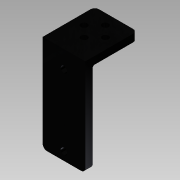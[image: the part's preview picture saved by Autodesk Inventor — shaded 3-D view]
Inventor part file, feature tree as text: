
AUTODESK INVENTOR PART (.ipt)
format: ipt  version: 2015 SP1 (Build 190203100, 203)  size: 181,760 bytes
history: native  units: mm
features: sketch x8, extrude x6, projected_geometry x3, sweep x1, fillet x1
ambient origin geometry x8: Origin, YZ Plane, XZ Plane, XY Plane, X Axis, Y Axis, Z Axis, Center Point
bodies: Solid1 (feature_tree)
feature tree (19):
  extrude  "Extrusion1"  Depth=20.0mm
  sweep  "Sweep1"
  extrude  "Extrusion2"  TaperAngle=0.0deg  [1 undecoded]
  fillet  "Fillet1"  Radius=20.0mm
  extrude  "Extrusion3"  Depth=1.0mm
  extrude  "Extrusion4"  Depth=3.0mm
  extrude  "Extrusion5"  Depth=2.0mm TaperAngle=0.0deg
  extrude  "Extrusion6"  Depth=2.0mm
  sketch  "Sketch1"  dims[d0=20.0mm d1=40.0mm]
  sketch  "Sketch2"  dims[d2=2.0mm d3=2.0mm d4=0.0mm]
  sketch  "Sketch3"  dims[d5=2.0mm d6=0.0mm d7=0.0mm d8=20.0mm]
  projected_geometry  "Projected Loop1"
  sketch  "Sketch4"  dims[d9=1.0mm d10=3.0mm]
  sketch  "Sketch5"  dims[d11=3.0mm d12=3.0mm]
  sketch  "Sketch7"  dims[d13=3.0mm d14=2.0mm d15=0.0mm]
  sketch  "Sketch9"  dims[d16=2.0mm d17=3.0mm d18=3.0mm d19=33.33mm]
  projected_geometry  "Projected Loop2"
  sketch  "Sketch10"  dims[d20=2.0mm d21=0.0mm d23=20.0mm d24=0.0mm d25=1.5mm d26=0.0mm d27=1.5mm d28=0.0mm]
  projected_geometry  "Projected Loop3"
note: 1 required parameter value undecoded (feature->parameter linkage not recoverable at this tier; creation-order binding heuristic only, values carry confidence <= 0.55)
